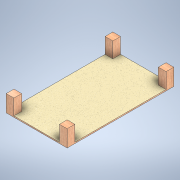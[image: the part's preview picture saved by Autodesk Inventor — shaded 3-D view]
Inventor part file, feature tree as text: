
AUTODESK INVENTOR PART (.ipt)
format: ipt  version: 2022 (Build 260153070, 153G)  size: 140,288 bytes
history: native  units: in
note: dims shown in document units (in); Inventor stores cm internally (conversion verified against a paired STEP export)
features: extrude x2, sketch x2
ambient origin geometry x8: Origin, YZ Plane, XZ Plane, XY Plane, X Axis, Y Axis, Z Axis, Center Point
bodies: Solid1 (feature_tree)
feature tree (4):
  extrude  "Extrusion1"  Depth=15.748in
  extrude  "Extrusion2"  Depth=2.0in
  sketch  "Sketch1"  dims[d0=27.5591in d1=15.748in]
  sketch  "Sketch2"  dims[d2=0.315in d3=0.0in d4=2.0in d5=2.0in d6=2.0in d7=2.0in d8=2.0in d9=2.0in d10=2.0in d11=4.0in d12=0.0in]
